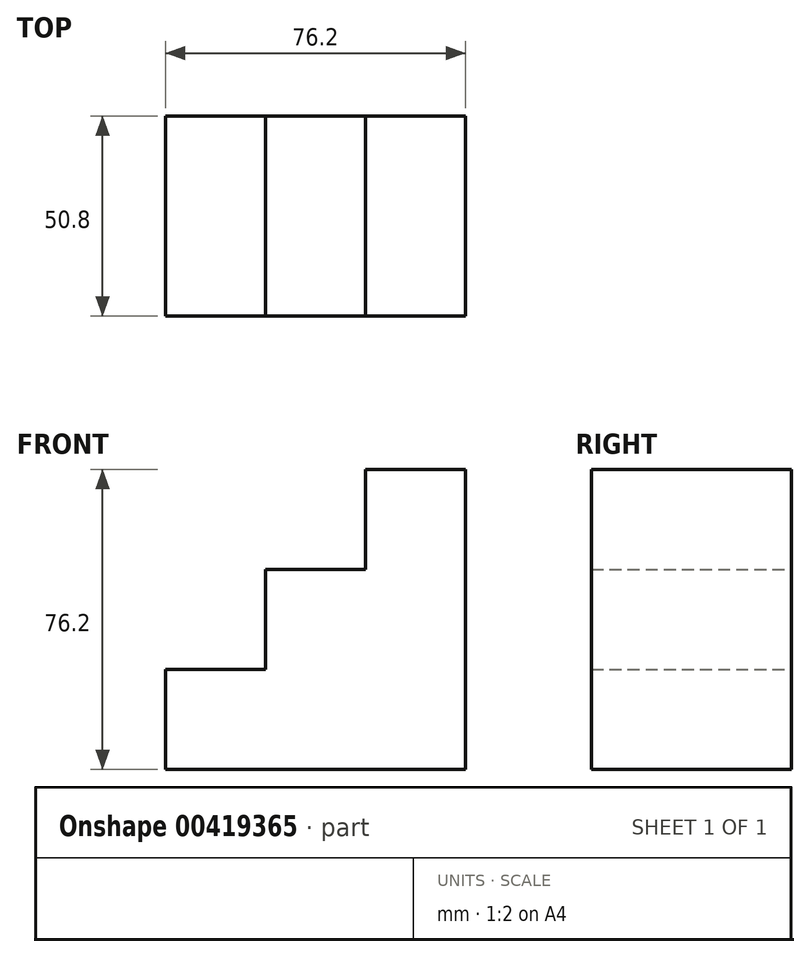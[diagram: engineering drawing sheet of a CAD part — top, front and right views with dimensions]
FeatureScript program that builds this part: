
annotation { "Feature Type Name" : "Feature", "Feature Type Description" : "" }
export const myFeature = defineFeature(function(context is Context, id is Id, definition is map)
    precondition{}
    {
        {
            var Q0;
            Q0=qCreatedBy(makeId("Front.planeOp"),FACE);
            var sketch = newSketch(context, id + "F0", { "sketchPlane" : qUnion([Q0])});
            skLineSegment(sketch, "E0", {"start": v(0, -21) * mm, "end": v(76.2, -21) * mm});
            skLineSegment(sketch, "E1", {"start": v(76.2, -21) * mm, "end": v(76.2, 55.2) * mm});
            skLineSegment(sketch, "E2", {"start": v(76.2, 55.2) * mm, "end": v(50.8, 55.2) * mm});
            skLineSegment(sketch, "E3", {"start": v(50.8, 55.2) * mm, "end": v(50.8, 29.8) * mm});
            skLineSegment(sketch, "E4", {"start": v(50.8, 29.8) * mm, "end": v(25.4, 29.8) * mm});
            skLineSegment(sketch, "E5", {"start": v(25.4, 29.8) * mm, "end": v(25.4, 4.4) * mm});
            skLineSegment(sketch, "E6", {"start": v(25.4, 4.4) * mm, "end": v(0, 4.4) * mm});
            skLineSegment(sketch, "E7", {"start": v(0, 4.4) * mm, "end": v(0, -21) * mm});
            skSolve(sketch);
        }
        {
            var Q0;
            Q0 = qSketchRegion(id + "F0", true);
            extrude(context, id + "F1", {"entities" : qUnion([Q0]), "depth" : 50.8 * mm});
        }
    });
